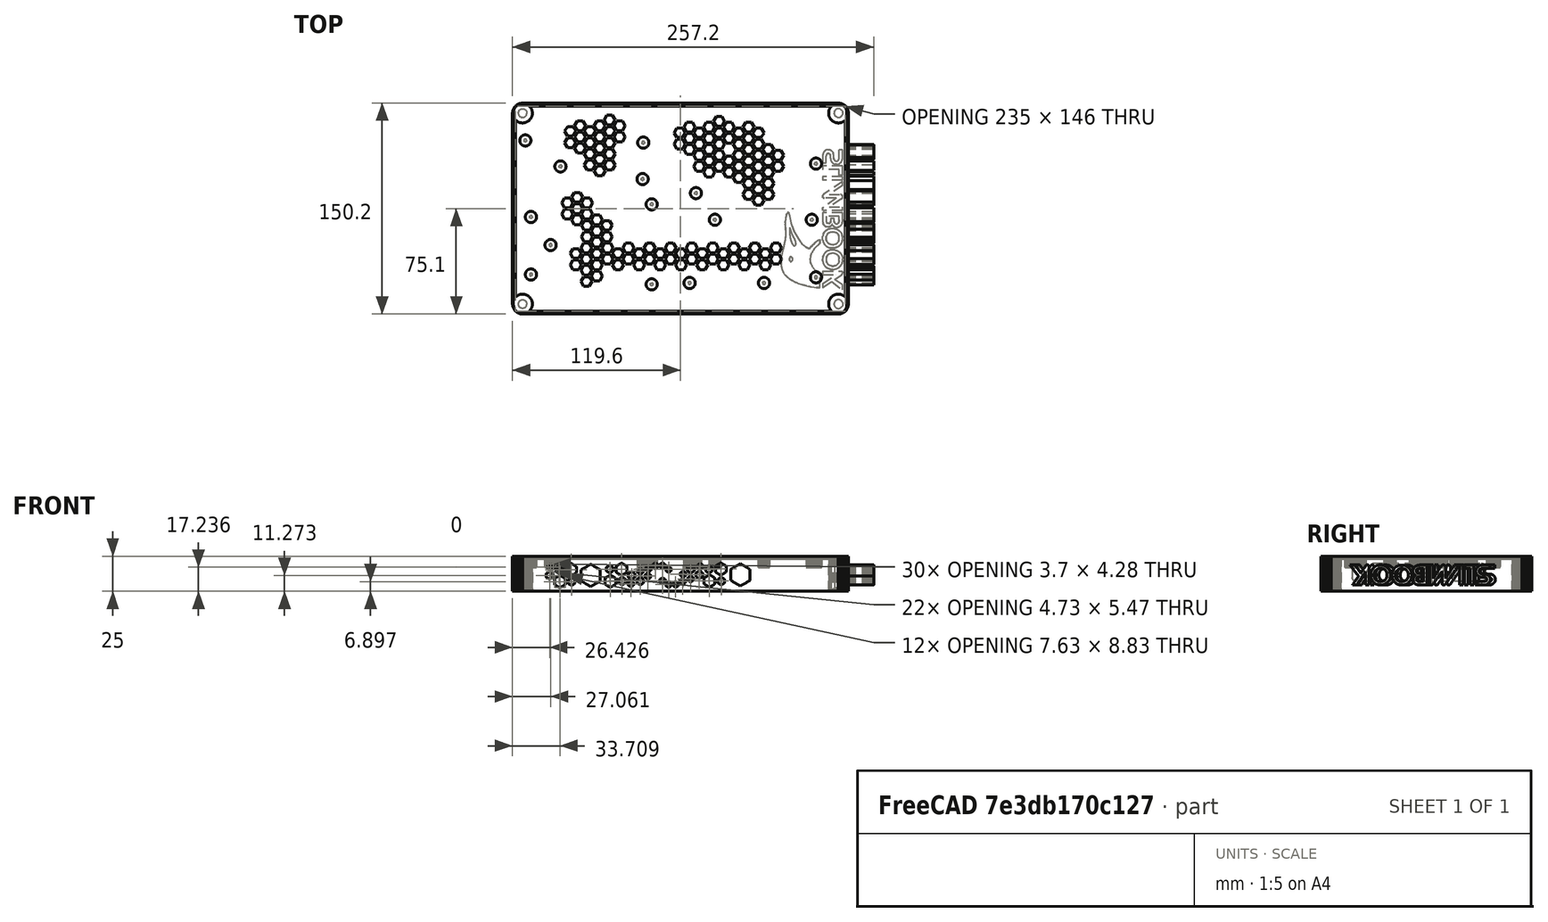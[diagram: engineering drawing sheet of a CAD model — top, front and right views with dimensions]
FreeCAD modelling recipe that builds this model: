
FCSTD DOCUMENT  (FreeCAD 0.21R33771 (Git))
Label: CAJA_slimbook
License: All rights reserved
LicenseURL: http://en.wikipedia.org/wiki/All_rights_reserved
objects: Part::Feature×108, Part::Extrusion×84, Part::Face×22, Part::Cut×8, Part::MultiFuse×5
note: 227 computed .brp shape members not serialized (recipe doc carries the construction recipe); baked Part::Feature solids carry a one-line shape summary decoded from their .brp

FEATURE [Part::Feature] path4723020
  shape: bbox 20.8 x 14.35 x 2.667e-07 mm, 0 faces, 0 solids (baked)
FEATURE [Part::Face] Face
  FaceMakerClass = Part::FaceMakerBullseye
  Sources = -> [path4723020]
FEATURE [Part::Extrusion] Extrude101
  Base = -> Face
  Dir = (0,0,1)
  DirMode = 2
  FaceMakerClass = Part::FaceMakerBullseye
  LengthFwd = 20
  LengthRev = 0
  Placement = pos=(235.5,118.54,-29.31) rot=(0.57735,-0.57735,0.57735;4.18879rad)
  Solid = false
  Symmetric = false
FEATURE [Part::Feature] path4723021
  shape: bbox 13.53 x 14.33 x 2.667e-07 mm, 0 faces, 0 solids (baked)
FEATURE [Part::Face] Face016
  FaceMakerClass = Part::FaceMakerBullseye
  Sources = -> [path4723021]
FEATURE [Part::Extrusion] Extrude102
  Base = -> Face016
  Dir = (0,0,1)
  DirMode = 2
  FaceMakerClass = Part::FaceMakerBullseye
  LengthFwd = 20
  LengthRev = 0
  Placement = pos=(235.5,118.54,-29.31) rot=(0.57735,-0.57735,0.57735;4.18879rad)
  Solid = false
  Symmetric = false
FEATURE [Part::Feature] path4723022
  shape: bbox 14.02 x 14.18 x 2.667e-07 mm, 0 faces, 0 solids (baked)
FEATURE [Part::Face] Face024
  FaceMakerClass = Part::FaceMakerBullseye
  Sources = -> [path4723022]
FEATURE [Part::Feature] path4723023
  shape: bbox 10.29 x 14.24 x 2.667e-07 mm, 0 faces, 0 solids (baked)
FEATURE [Part::Face] Face022
  FaceMakerClass = Part::FaceMakerBullseye
  Sources = -> [path4723023]
FEATURE [Part::Feature] path4723024
  shape: bbox 10.44 x 14.24 x 2.667e-07 mm, 0 faces, 0 solids (baked)
FEATURE [Part::Face] Face021
  FaceMakerClass = Part::FaceMakerBullseye
  Sources = -> [path4723024]
FEATURE [Part::Extrusion] Extrude106
  Base = -> Face021
  Dir = (0,0,1)
  DirMode = 2
  FaceMakerClass = Part::FaceMakerBullseye
  LengthFwd = 20
  LengthRev = 0
  Placement = pos=(235.5,118.54,-29.31) rot=(0.57735,-0.57735,0.57735;4.18879rad)
  Solid = false
  Symmetric = false
FEATURE [Part::Feature] path4723025
  shape: bbox 6.55 x 14.24 x 2.667e-07 mm, 0 faces, 0 solids (baked)
FEATURE [Part::Face] Face019
  FaceMakerClass = Part::FaceMakerBullseye
  Sources = -> [path4723025]
FEATURE [Part::Extrusion] Extrude104
  Base = -> Face019
  Dir = (0,0,1)
  DirMode = 2
  FaceMakerClass = Part::FaceMakerBullseye
  LengthFwd = 20
  LengthRev = 0
  Placement = pos=(235.5,118.54,-29.31) rot=(0.57735,-0.57735,0.57735;4.18879rad)
  Solid = false
  Symmetric = false
FEATURE [Part::Feature] path4723026
  shape: bbox 2.568 x 14.24 x 2.667e-07 mm, 0 faces, 0 solids (baked)
FEATURE [Part::Face] Face020
  FaceMakerClass = Part::FaceMakerBullseye
  Sources = -> [path4723026]
FEATURE [Part::Extrusion] Extrude105
  Base = -> Face020
  Dir = (0,0,1)
  DirMode = 2
  FaceMakerClass = Part::FaceMakerBullseye
  LengthFwd = 20
  LengthRev = 0
  Placement = pos=(235.5,118.54,-29.31) rot=(0.57735,-0.57735,0.57735;4.18879rad)
  Solid = false
  Symmetric = false
FEATURE [Part::Feature] path4723027  label="O"
  shape: bbox 14.02 x 14.24 x 2.667e-07 mm, 0 faces, 0 solids (baked)
FEATURE [Part::Face] Face018
  FaceMakerClass = Part::FaceMakerBullseye
  Sources = -> [path4723027]
FEATURE [Part::Feature] path4723028  label="b"
  shape: bbox 5.247 x 9.291 x 2.667e-07 mm, 0 faces, 0 solids (baked)
FEATURE [Part::Face] Face023
  FaceMakerClass = Part::FaceMakerBullseye
  Sources = -> [path4723028]
FEATURE [Part::Cut] Cut042
  Base = -> Face022
  Refine = true
  Tool = -> Face023
FEATURE [Part::Extrusion] Extrude107
  Base = -> Cut042
  Dir = (0,0,1)
  DirMode = 2
  FaceMakerClass = Part::FaceMakerBullseye
  LengthFwd = 20
  LengthRev = 0
  Placement = pos=(235.5,118.54,-29.31) rot=(0.57735,-0.57735,0.57735;4.18879rad)
  Solid = false
  Symmetric = false
FEATURE [Part::Feature] path4723029  label="oo"
  shape: bbox 9.343 x 9.236 x 2.667e-07 mm, 0 faces, 0 solids (baked)
FEATURE [Part::Face] Face025
  FaceMakerClass = Part::FaceMakerBullseye
  Sources = -> [path4723029]
FEATURE [Part::Cut] Cut043
  Base = -> Face024
  Refine = true
  Tool = -> Face025
FEATURE [Part::Extrusion] Extrude108
  Base = -> Cut043
  Dir = (0,0,1)
  DirMode = 2
  FaceMakerClass = Part::FaceMakerBullseye
  LengthFwd = 20
  LengthRev = 0
  Placement = pos=(235.5,118.54,-29.31) rot=(0.57735,-0.57735,0.57735;4.18879rad)
  Solid = false
  Symmetric = false
FEATURE [Part::Feature] path4723030
  shape: bbox 9.342 x 9.272 x 2.667e-07 mm, 0 faces, 0 solids (baked)
FEATURE [Part::Face] Face017  label="o"
  FaceMakerClass = Part::FaceMakerBullseye
  Sources = -> [path4723030]
FEATURE [Part::Cut] Cut041
  Base = -> Face018
  Refine = true
  Tool = -> Face017
FEATURE [Part::Extrusion] Extrude103
  Base = -> Cut041
  Dir = (0,0,1)
  DirMode = 2
  FaceMakerClass = Part::FaceMakerBullseye
  LengthFwd = 20
  LengthRev = 0
  Placement = pos=(235.5,118.54,-29.31) rot=(0.57735,-0.57735,0.57735;4.18879rad)
  Solid = false
  Symmetric = false
FEATURE [Part::MultiFuse] Fusion028  label="palabra"
  Placement = pos=(0.5,3.5,0) rot=(0,0,1;0rad)
  Refine = true
  Shapes = -> [Extrude101,Extrude102,Extrude103,Extrude104,Extrude105,Extrude106,Extrude107,Extrude108]
FEATURE [Part::Feature] path4723031
  shape: bbox 20.8 x 14.35 x 2.667e-07 mm, 0 faces, 0 solids (baked)
FEATURE [Part::Face] Face026
  FaceMakerClass = Part::FaceMakerBullseye
  Sources = -> [path4723031]
FEATURE [Part::Extrusion] Extrude109
  Base = -> Face026
  Dir = (0,0,1)
  DirMode = 2
  FaceMakerClass = Part::FaceMakerBullseye
  LengthFwd = 20
  LengthRev = 0
  Placement = pos=(235.5,118.54,-29.31) rot=(0.57735,-0.57735,0.57735;4.18879rad)
  Solid = false
  Symmetric = false
FEATURE [Part::Feature] path4723032
  shape: bbox 13.53 x 14.33 x 2.667e-07 mm, 0 faces, 0 solids (baked)
FEATURE [Part::Face] Face027
  FaceMakerClass = Part::FaceMakerBullseye
  Sources = -> [path4723032]
FEATURE [Part::Extrusion] Extrude110
  Base = -> Face027
  Dir = (0,0,1)
  DirMode = 2
  FaceMakerClass = Part::FaceMakerBullseye
  LengthFwd = 20
  LengthRev = 0
  Placement = pos=(235.5,118.54,-29.31) rot=(0.57735,-0.57735,0.57735;4.18879rad)
  Solid = false
  Symmetric = false
FEATURE [Part::Feature] path4723033
  shape: bbox 14.02 x 14.18 x 2.667e-07 mm, 0 faces, 0 solids (baked)
FEATURE [Part::Face] Face035
  FaceMakerClass = Part::FaceMakerBullseye
  Sources = -> [path4723033]
FEATURE [Part::Feature] path4723034
  shape: bbox 10.29 x 14.24 x 2.667e-07 mm, 0 faces, 0 solids (baked)
FEATURE [Part::Face] Face033
  FaceMakerClass = Part::FaceMakerBullseye
  Sources = -> [path4723034]
FEATURE [Part::Feature] path4723035
  shape: bbox 10.44 x 14.24 x 2.667e-07 mm, 0 faces, 0 solids (baked)
FEATURE [Part::Face] Face032
  FaceMakerClass = Part::FaceMakerBullseye
  Sources = -> [path4723035]
FEATURE [Part::Extrusion] Extrude114
  Base = -> Face032
  Dir = (0,0,1)
  DirMode = 2
  FaceMakerClass = Part::FaceMakerBullseye
  LengthFwd = 20
  LengthRev = 0
  Placement = pos=(235.5,118.54,-29.31) rot=(0.57735,-0.57735,0.57735;4.18879rad)
  Solid = false
  Symmetric = false
FEATURE [Part::Feature] path4723036
  shape: bbox 6.55 x 14.24 x 2.667e-07 mm, 0 faces, 0 solids (baked)
FEATURE [Part::Face] Face030
  FaceMakerClass = Part::FaceMakerBullseye
  Sources = -> [path4723036]
FEATURE [Part::Extrusion] Extrude112
  Base = -> Face030
  Dir = (0,0,1)
  DirMode = 2
  FaceMakerClass = Part::FaceMakerBullseye
  LengthFwd = 20
  LengthRev = 0
  Placement = pos=(235.5,118.54,-29.31) rot=(0.57735,-0.57735,0.57735;4.18879rad)
  Solid = false
  Symmetric = false
FEATURE [Part::Feature] path4723037
  shape: bbox 2.568 x 14.24 x 2.667e-07 mm, 0 faces, 0 solids (baked)
FEATURE [Part::Face] Face031
  FaceMakerClass = Part::FaceMakerBullseye
  Sources = -> [path4723037]
FEATURE [Part::Extrusion] Extrude113
  Base = -> Face031
  Dir = (0,0,1)
  DirMode = 2
  FaceMakerClass = Part::FaceMakerBullseye
  LengthFwd = 20
  LengthRev = 0
  Placement = pos=(235.5,118.54,-29.31) rot=(0.57735,-0.57735,0.57735;4.18879rad)
  Solid = false
  Symmetric = false
FEATURE [Part::Feature] path4723038  label="O001"
  shape: bbox 14.02 x 14.24 x 2.667e-07 mm, 0 faces, 0 solids (baked)
FEATURE [Part::Face] Face029
  FaceMakerClass = Part::FaceMakerBullseye
  Sources = -> [path4723038]
FEATURE [Part::Feature] path4723039  label="b001"
  shape: bbox 5.247 x 9.291 x 2.667e-07 mm, 0 faces, 0 solids (baked)
FEATURE [Part::Face] Face034
  FaceMakerClass = Part::FaceMakerBullseye
  Sources = -> [path4723039]
FEATURE [Part::Cut] Cut045
  Base = -> Face033
  Refine = true
  Tool = -> Face034
FEATURE [Part::Extrusion] Extrude115
  Base = -> Cut045
  Dir = (0,0,1)
  DirMode = 2
  FaceMakerClass = Part::FaceMakerBullseye
  LengthFwd = 20
  LengthRev = 0
  Placement = pos=(235.5,118.54,-29.31) rot=(0.57735,-0.57735,0.57735;4.18879rad)
  Solid = false
  Symmetric = false
FEATURE [Part::Feature] path4723040  label="oo001"
  shape: bbox 9.343 x 9.236 x 2.667e-07 mm, 0 faces, 0 solids (baked)
FEATURE [Part::Face] Face036
  FaceMakerClass = Part::FaceMakerBullseye
  Sources = -> [path4723040]
FEATURE [Part::Cut] Cut046
  Base = -> Face035
  Refine = true
  Tool = -> Face036
FEATURE [Part::Extrusion] Extrude116
  Base = -> Cut046
  Dir = (0,0,1)
  DirMode = 2
  FaceMakerClass = Part::FaceMakerBullseye
  LengthFwd = 20
  LengthRev = 0
  Placement = pos=(235.5,118.54,-29.31) rot=(0.57735,-0.57735,0.57735;4.18879rad)
  Solid = false
  Symmetric = false
FEATURE [Part::Feature] path4723041
  shape: bbox 9.342 x 9.272 x 2.667e-07 mm, 0 faces, 0 solids (baked)
FEATURE [Part::Face] Face028  label="o001"
  FaceMakerClass = Part::FaceMakerBullseye
  Sources = -> [path4723041]
FEATURE [Part::Cut] Cut044
  Base = -> Face029
  Refine = true
  Tool = -> Face028
FEATURE [Part::Extrusion] Extrude111
  Base = -> Cut044
  Dir = (0,0,1)
  DirMode = 2
  FaceMakerClass = Part::FaceMakerBullseye
  LengthFwd = 20
  LengthRev = 0
  Placement = pos=(235.5,118.54,-29.31) rot=(0.57735,-0.57735,0.57735;4.18879rad)
  Solid = false
  Symmetric = false
FEATURE [Part::Feature] path2951
  shape: bbox 3.697 x 4.275 x 7.858e-07 mm, 0 faces, 0 solids (baked)
FEATURE [Part::Feature] path4723042
  shape: bbox 3.697 x 4.275 x 7.858e-07 mm, 0 faces, 0 solids (baked)
FEATURE [Part::Feature] path4723043
  shape: bbox 7.634 x 8.828 x 7.858e-07 mm, 0 faces, 0 solids (baked)
FEATURE [Part::Feature] path4723044
  shape: bbox 7.634 x 8.828 x 7.858e-07 mm, 0 faces, 0 solids (baked)
FEATURE [Part::Feature] path4723045
  shape: bbox 7.635 x 8.827 x 7.858e-07 mm, 0 faces, 0 solids (baked)
FEATURE [Part::Feature] path4723046
  shape: bbox 3.697 x 4.276 x 7.858e-07 mm, 0 faces, 0 solids (baked)
FEATURE [Part::Feature] path4723047
  shape: bbox 13.76 x 15.91 x 7.858e-07 mm, 0 faces, 0 solids (baked)
FEATURE [Part::Feature] path4723048
  shape: bbox 3.697 x 4.275 x 7.858e-07 mm, 0 faces, 0 solids (baked)
FEATURE [Part::Feature] path4723049
  shape: bbox 13.76 x 15.91 x 7.858e-07 mm, 0 faces, 0 solids (baked)
FEATURE [Part::Feature] path4723050
  shape: bbox 4.734 x 5.474 x 7.858e-07 mm, 0 faces, 0 solids (baked)
FEATURE [Part::Feature] path4723051
  shape: bbox 4.734 x 5.474 x 7.858e-07 mm, 0 faces, 0 solids (baked)
FEATURE [Part::Feature] path4723052
  shape: bbox 4.734 x 5.474 x 7.858e-07 mm, 0 faces, 0 solids (baked)
FEATURE [Part::Feature] path4723053
  shape: bbox 3.697 x 4.276 x 7.858e-07 mm, 0 faces, 0 solids (baked)
FEATURE [Part::Feature] path4723054
  shape: bbox 4.734 x 5.474 x 7.858e-07 mm, 0 faces, 0 solids (baked)
FEATURE [Part::Feature] path4723055
  shape: bbox 3.697 x 4.275 x 7.858e-07 mm, 0 faces, 0 solids (baked)
FEATURE [Part::Feature] path4723056
  shape: bbox 3.697 x 4.275 x 7.858e-07 mm, 0 faces, 0 solids (baked)
FEATURE [Part::Feature] path4723057
  shape: bbox 4.734 x 5.474 x 7.858e-07 mm, 0 faces, 0 solids (baked)
FEATURE [Part::Feature] path4723058
  shape: bbox 3.697 x 4.276 x 7.858e-07 mm, 0 faces, 0 solids (baked)
FEATURE [Part::Feature] path4723059
  shape: bbox 4.734 x 5.474 x 7.858e-07 mm, 0 faces, 0 solids (baked)
FEATURE [Part::Feature] path4723060
  shape: bbox 4.734 x 5.474 x 7.858e-07 mm, 0 faces, 0 solids (baked)
FEATURE [Part::Feature] path4723061
  shape: bbox 3.697 x 4.275 x 7.858e-07 mm, 0 faces, 0 solids (baked)
FEATURE [Part::Feature] path4723062
  shape: bbox 7.634 x 8.828 x 7.858e-07 mm, 0 faces, 0 solids (baked)
FEATURE [Part::Feature] path4723063
  shape: bbox 7.634 x 8.827 x 7.858e-07 mm, 0 faces, 0 solids (baked)
FEATURE [Part::Feature] path4723064
  shape: bbox 7.634 x 8.828 x 7.858e-07 mm, 0 faces, 0 solids (baked)
FEATURE [Part::Feature] path4723065
  shape: bbox 3.697 x 4.276 x 7.858e-07 mm, 0 faces, 0 solids (baked)
FEATURE [Part::Feature] path4723066
  shape: bbox 4.734 x 5.474 x 7.858e-07 mm, 0 faces, 0 solids (baked)
FEATURE [Part::Feature] path4723067
  shape: bbox 4.734 x 5.474 x 7.858e-07 mm, 0 faces, 0 solids (baked)
FEATURE [Part::Feature] path4723068
  shape: bbox 4.734 x 5.474 x 7.858e-07 mm, 0 faces, 0 solids (baked)
FEATURE [Part::Feature] path4723069
  shape: bbox 3.697 x 4.275 x 7.858e-07 mm, 0 faces, 0 solids (baked)
FEATURE [Part::Feature] path4723070
  shape: bbox 4.734 x 5.474 x 7.858e-07 mm, 0 faces, 0 solids (baked)
FEATURE [Part::Feature] path4723071
  shape: bbox 3.697 x 4.275 x 7.858e-07 mm, 0 faces, 0 solids (baked)
FEATURE [Part::Feature] path4723072
  shape: bbox 3.697 x 4.275 x 7.858e-07 mm, 0 faces, 0 solids (baked)
FEATURE [Part::Feature] path4723073
  shape: bbox 3.697 x 4.275 x 7.858e-07 mm, 0 faces, 0 solids (baked)
FEATURE [Part::Feature] path4723074
  shape: bbox 3.697 x 4.276 x 7.858e-07 mm, 0 faces, 0 solids (baked)
FEATURE [Part::Extrusion] Extrude
  Base = -> path4723042
  Dir = (0,0,1)
  DirMode = 2
  FaceMakerClass = Part::FaceMakerBullseye
  LengthFwd = 20
  LengthRev = 0
  Solid = true
  Symmetric = false
FEATURE [Part::Extrusion] Extrude117
  Base = -> path4723043
  Dir = (0,0,1)
  DirMode = 2
  FaceMakerClass = Part::FaceMakerBullseye
  LengthFwd = 20
  LengthRev = 0
  Solid = true
  Symmetric = false
FEATURE [Part::Extrusion] Extrude118
  Base = -> path4723044
  Dir = (0,0,1)
  DirMode = 2
  FaceMakerClass = Part::FaceMakerBullseye
  LengthFwd = 20
  LengthRev = 0
  Solid = true
  Symmetric = false
FEATURE [Part::Extrusion] Extrude119
  Base = -> path4723045
  Dir = (0,0,1)
  DirMode = 2
  FaceMakerClass = Part::FaceMakerBullseye
  LengthFwd = 20
  LengthRev = 0
  Solid = true
  Symmetric = false
FEATURE [Part::Extrusion] Extrude120
  Base = -> path4723046
  Dir = (0,0,1)
  DirMode = 2
  FaceMakerClass = Part::FaceMakerBullseye
  LengthFwd = 20
  LengthRev = 0
  Solid = true
  Symmetric = false
FEATURE [Part::Extrusion] Extrude121
  Base = -> path4723047
  Dir = (0,0,1)
  DirMode = 2
  FaceMakerClass = Part::FaceMakerBullseye
  LengthFwd = 20
  LengthRev = 0
  Solid = true
  Symmetric = false
FEATURE [Part::Extrusion] Extrude122
  Base = -> path4723048
  Dir = (0,0,1)
  DirMode = 2
  FaceMakerClass = Part::FaceMakerBullseye
  LengthFwd = 20
  LengthRev = 0
  Solid = true
  Symmetric = false
FEATURE [Part::Extrusion] Extrude123
  Base = -> path4723049
  Dir = (0,0,1)
  DirMode = 2
  FaceMakerClass = Part::FaceMakerBullseye
  LengthFwd = 20
  LengthRev = 0
  Solid = true
  Symmetric = false
FEATURE [Part::Extrusion] Extrude124
  Base = -> path4723050
  Dir = (0,0,1)
  DirMode = 2
  FaceMakerClass = Part::FaceMakerBullseye
  LengthFwd = 20
  LengthRev = 0
  Solid = true
  Symmetric = false
FEATURE [Part::Extrusion] Extrude125
  Base = -> path4723051
  Dir = (0,0,1)
  DirMode = 2
  FaceMakerClass = Part::FaceMakerBullseye
  LengthFwd = 20
  LengthRev = 0
  Solid = true
  Symmetric = false
FEATURE [Part::Extrusion] Extrude126
  Base = -> path4723052
  Dir = (0,0,1)
  DirMode = 2
  FaceMakerClass = Part::FaceMakerBullseye
  LengthFwd = 20
  LengthRev = 0
  Solid = true
  Symmetric = false
FEATURE [Part::Extrusion] Extrude127
  Base = -> path4723053
  Dir = (0,0,1)
  DirMode = 2
  FaceMakerClass = Part::FaceMakerBullseye
  LengthFwd = 20
  LengthRev = 0
  Solid = true
  Symmetric = false
FEATURE [Part::Extrusion] Extrude128
  Base = -> path4723054
  Dir = (0,0,1)
  DirMode = 2
  FaceMakerClass = Part::FaceMakerBullseye
  LengthFwd = 20
  LengthRev = 0
  Solid = true
  Symmetric = false
FEATURE [Part::Extrusion] Extrude129
  Base = -> path4723055
  Dir = (0,0,1)
  DirMode = 2
  FaceMakerClass = Part::FaceMakerBullseye
  LengthFwd = 20
  LengthRev = 0
  Solid = true
  Symmetric = false
FEATURE [Part::Extrusion] Extrude130
  Base = -> path4723056
  Dir = (0,0,1)
  DirMode = 2
  FaceMakerClass = Part::FaceMakerBullseye
  LengthFwd = 20
  LengthRev = 0
  Solid = true
  Symmetric = false
FEATURE [Part::Extrusion] Extrude131
  Base = -> path4723057
  Dir = (0,0,1)
  DirMode = 2
  FaceMakerClass = Part::FaceMakerBullseye
  LengthFwd = 20
  LengthRev = 0
  Solid = true
  Symmetric = false
FEATURE [Part::Extrusion] Extrude132
  Base = -> path4723058
  Dir = (0,0,1)
  DirMode = 2
  FaceMakerClass = Part::FaceMakerBullseye
  LengthFwd = 20
  LengthRev = 0
  Solid = true
  Symmetric = false
FEATURE [Part::Extrusion] Extrude133
  Base = -> path4723059
  Dir = (0,0,1)
  DirMode = 2
  FaceMakerClass = Part::FaceMakerBullseye
  LengthFwd = 20
  LengthRev = 0
  Solid = true
  Symmetric = false
FEATURE [Part::Extrusion] Extrude134
  Base = -> path4723060
  Dir = (0,0,1)
  DirMode = 2
  FaceMakerClass = Part::FaceMakerBullseye
  LengthFwd = 20
  LengthRev = 0
  Solid = true
  Symmetric = false
FEATURE [Part::Extrusion] Extrude135
  Base = -> path4723061
  Dir = (0,0,1)
  DirMode = 2
  FaceMakerClass = Part::FaceMakerBullseye
  LengthFwd = 20
  LengthRev = 0
  Solid = true
  Symmetric = false
FEATURE [Part::Extrusion] Extrude136
  Base = -> path4723062
  Dir = (0,0,1)
  DirMode = 2
  FaceMakerClass = Part::FaceMakerBullseye
  LengthFwd = 20
  LengthRev = 0
  Solid = true
  Symmetric = false
FEATURE [Part::Extrusion] Extrude137
  Base = -> path4723063
  Dir = (0,0,1)
  DirMode = 2
  FaceMakerClass = Part::FaceMakerBullseye
  LengthFwd = 20
  LengthRev = 0
  Solid = true
  Symmetric = false
FEATURE [Part::Extrusion] Extrude138
  Base = -> path4723064
  Dir = (0,0,1)
  DirMode = 2
  FaceMakerClass = Part::FaceMakerBullseye
  LengthFwd = 20
  LengthRev = 0
  Solid = true
  Symmetric = false
FEATURE [Part::Extrusion] Extrude139
  Base = -> path4723065
  Dir = (0,0,1)
  DirMode = 2
  FaceMakerClass = Part::FaceMakerBullseye
  LengthFwd = 20
  LengthRev = 0
  Solid = true
  Symmetric = false
FEATURE [Part::Extrusion] Extrude140
  Base = -> path4723066
  Dir = (0,0,1)
  DirMode = 2
  FaceMakerClass = Part::FaceMakerBullseye
  LengthFwd = 20
  LengthRev = 0
  Solid = true
  Symmetric = false
FEATURE [Part::Extrusion] Extrude141
  Base = -> path4723067
  Dir = (0,0,1)
  DirMode = 2
  FaceMakerClass = Part::FaceMakerBullseye
  LengthFwd = 20
  LengthRev = 0
  Solid = true
  Symmetric = false
FEATURE [Part::Extrusion] Extrude142
  Base = -> path4723068
  Dir = (0,0,1)
  DirMode = 2
  FaceMakerClass = Part::FaceMakerBullseye
  LengthFwd = 20
  LengthRev = 0
  Solid = true
  Symmetric = false
FEATURE [Part::Extrusion] Extrude143
  Base = -> path4723069
  Dir = (0,0,1)
  DirMode = 2
  FaceMakerClass = Part::FaceMakerBullseye
  LengthFwd = 20
  LengthRev = 0
  Solid = true
  Symmetric = false
FEATURE [Part::Extrusion] Extrude144
  Base = -> path4723070
  Dir = (0,0,1)
  DirMode = 2
  FaceMakerClass = Part::FaceMakerBullseye
  LengthFwd = 20
  LengthRev = 0
  Solid = true
  Symmetric = false
FEATURE [Part::Extrusion] Extrude145
  Base = -> path4723071
  Dir = (0,0,1)
  DirMode = 2
  FaceMakerClass = Part::FaceMakerBullseye
  LengthFwd = 20
  LengthRev = 0
  Solid = true
  Symmetric = false
FEATURE [Part::Extrusion] Extrude146
  Base = -> path4723072
  Dir = (0,0,1)
  DirMode = 2
  FaceMakerClass = Part::FaceMakerBullseye
  LengthFwd = 20
  LengthRev = 0
  Solid = true
  Symmetric = false
FEATURE [Part::Extrusion] Extrude147
  Base = -> path4723073
  Dir = (0,0,1)
  DirMode = 2
  FaceMakerClass = Part::FaceMakerBullseye
  LengthFwd = 20
  LengthRev = 0
  Solid = true
  Symmetric = false
FEATURE [Part::Extrusion] Extrude148
  Base = -> path4723074
  Dir = (0,0,1)
  DirMode = 2
  FaceMakerClass = Part::FaceMakerBullseye
  LengthFwd = 20
  LengthRev = 0
  Solid = true
  Symmetric = false
FEATURE [Part::Extrusion] Extrude149
  Base = -> path2951
  Dir = (0,0,1)
  DirMode = 2
  FaceMakerClass = Part::FaceMakerBullseye
  LengthFwd = 20
  LengthRev = 0
  Solid = true
  Symmetric = false
FEATURE [Part::MultiFuse] Fusion  label="palitos_cortos"
  Placement = pos=(105,160,17) rot=(1,0,0;1.5708rad)
  Refine = true
  Shapes = -> [Extrude,Extrude117,Extrude118,Extrude119,Extrude120,Extrude121,Extrude122,Extrude123,Extrude124,Extrude125,Extrude126,Extrude127,Extrude128,Extrude129,Extrude130,Extrude131,Extrude132,Extrude133,Extrude134,Extrude135,Extrude136,Extrude137,Extrude138,Extrude139,Extrude140,Extrude141,Extrude142,Extrude143,Extrude144,Extrude145,Extrude146,Extrude147,Extrude148,Extrude149]
  expr: .Placement.Rotation.Angle = 90
FEATURE [Part::Feature] path4723109
  shape: bbox 3.697 x 4.275 x 7.858e-07 mm, 0 faces, 0 solids (baked)
FEATURE [Part::Extrusion] Extrude217
  Base = -> path4723109
  Dir = (0,0,1)
  DirMode = 2
  FaceMakerClass = Part::FaceMakerBullseye
  LengthFwd = 20
  LengthRev = 0
  Solid = true
  Symmetric = false
FEATURE [Part::Feature] path4723110
  shape: bbox 3.697 x 4.275 x 7.858e-07 mm, 0 faces, 0 solids (baked)
FEATURE [Part::Extrusion] Extrude184
  Base = -> path4723110
  Dir = (0,0,1)
  DirMode = 2
  FaceMakerClass = Part::FaceMakerBullseye
  LengthFwd = 20
  LengthRev = 0
  Solid = true
  Symmetric = false
FEATURE [Part::Feature] path4723111
  shape: bbox 7.634 x 8.828 x 7.858e-07 mm, 0 faces, 0 solids (baked)
FEATURE [Part::Extrusion] Extrude185
  Base = -> path4723111
  Dir = (0,0,1)
  DirMode = 2
  FaceMakerClass = Part::FaceMakerBullseye
  LengthFwd = 20
  LengthRev = 0
  Solid = true
  Symmetric = false
FEATURE [Part::Feature] path4723112
  shape: bbox 7.634 x 8.828 x 7.858e-07 mm, 0 faces, 0 solids (baked)
FEATURE [Part::Extrusion] Extrude186
  Base = -> path4723112
  Dir = (0,0,1)
  DirMode = 2
  FaceMakerClass = Part::FaceMakerBullseye
  LengthFwd = 20
  LengthRev = 0
  Solid = true
  Symmetric = false
FEATURE [Part::Feature] path4723113
  shape: bbox 7.635 x 8.827 x 7.858e-07 mm, 0 faces, 0 solids (baked)
FEATURE [Part::Extrusion] Extrude187
  Base = -> path4723113
  Dir = (0,0,1)
  DirMode = 2
  FaceMakerClass = Part::FaceMakerBullseye
  LengthFwd = 20
  LengthRev = 0
  Solid = true
  Symmetric = false
FEATURE [Part::Feature] path4723114
  shape: bbox 3.697 x 4.276 x 7.858e-07 mm, 0 faces, 0 solids (baked)
FEATURE [Part::Extrusion] Extrude188
  Base = -> path4723114
  Dir = (0,0,1)
  DirMode = 2
  FaceMakerClass = Part::FaceMakerBullseye
  LengthFwd = 20
  LengthRev = 0
  Solid = true
  Symmetric = false
FEATURE [Part::Feature] path4723115
  shape: bbox 13.76 x 15.91 x 7.858e-07 mm, 0 faces, 0 solids (baked)
FEATURE [Part::Extrusion] Extrude189
  Base = -> path4723115
  Dir = (0,0,1)
  DirMode = 2
  FaceMakerClass = Part::FaceMakerBullseye
  LengthFwd = 20
  LengthRev = 0
  Solid = true
  Symmetric = false
FEATURE [Part::Feature] path4723116
  shape: bbox 3.697 x 4.275 x 7.858e-07 mm, 0 faces, 0 solids (baked)
FEATURE [Part::Extrusion] Extrude190
  Base = -> path4723116
  Dir = (0,0,1)
  DirMode = 2
  FaceMakerClass = Part::FaceMakerBullseye
  LengthFwd = 20
  LengthRev = 0
  Solid = true
  Symmetric = false
FEATURE [Part::Feature] path4723117
  shape: bbox 13.76 x 15.91 x 7.858e-07 mm, 0 faces, 0 solids (baked)
FEATURE [Part::Extrusion] Extrude191
  Base = -> path4723117
  Dir = (0,0,1)
  DirMode = 2
  FaceMakerClass = Part::FaceMakerBullseye
  LengthFwd = 20
  LengthRev = 0
  Solid = true
  Symmetric = false
FEATURE [Part::Feature] path4723118
  shape: bbox 4.734 x 5.474 x 7.858e-07 mm, 0 faces, 0 solids (baked)
FEATURE [Part::Extrusion] Extrude192
  Base = -> path4723118
  Dir = (0,0,1)
  DirMode = 2
  FaceMakerClass = Part::FaceMakerBullseye
  LengthFwd = 20
  LengthRev = 0
  Solid = true
  Symmetric = false
FEATURE [Part::Feature] path4723119
  shape: bbox 4.734 x 5.474 x 7.858e-07 mm, 0 faces, 0 solids (baked)
FEATURE [Part::Extrusion] Extrude193
  Base = -> path4723119
  Dir = (0,0,1)
  DirMode = 2
  FaceMakerClass = Part::FaceMakerBullseye
  LengthFwd = 20
  LengthRev = 0
  Solid = true
  Symmetric = false
FEATURE [Part::Feature] path4723120
  shape: bbox 4.734 x 5.474 x 7.858e-07 mm, 0 faces, 0 solids (baked)
FEATURE [Part::Extrusion] Extrude194
  Base = -> path4723120
  Dir = (0,0,1)
  DirMode = 2
  FaceMakerClass = Part::FaceMakerBullseye
  LengthFwd = 20
  LengthRev = 0
  Solid = true
  Symmetric = false
FEATURE [Part::Feature] path4723121
  shape: bbox 3.697 x 4.276 x 7.858e-07 mm, 0 faces, 0 solids (baked)
FEATURE [Part::Extrusion] Extrude195
  Base = -> path4723121
  Dir = (0,0,1)
  DirMode = 2
  FaceMakerClass = Part::FaceMakerBullseye
  LengthFwd = 20
  LengthRev = 0
  Solid = true
  Symmetric = false
FEATURE [Part::Feature] path4723122
  shape: bbox 4.734 x 5.474 x 7.858e-07 mm, 0 faces, 0 solids (baked)
FEATURE [Part::Extrusion] Extrude196
  Base = -> path4723122
  Dir = (0,0,1)
  DirMode = 2
  FaceMakerClass = Part::FaceMakerBullseye
  LengthFwd = 20
  LengthRev = 0
  Solid = true
  Symmetric = false
FEATURE [Part::Feature] path4723123
  shape: bbox 3.697 x 4.275 x 7.858e-07 mm, 0 faces, 0 solids (baked)
FEATURE [Part::Extrusion] Extrude197
  Base = -> path4723123
  Dir = (0,0,1)
  DirMode = 2
  FaceMakerClass = Part::FaceMakerBullseye
  LengthFwd = 20
  LengthRev = 0
  Solid = true
  Symmetric = false
FEATURE [Part::Feature] path4723124
  shape: bbox 3.697 x 4.275 x 7.858e-07 mm, 0 faces, 0 solids (baked)
FEATURE [Part::Extrusion] Extrude198
  Base = -> path4723124
  Dir = (0,0,1)
  DirMode = 2
  FaceMakerClass = Part::FaceMakerBullseye
  LengthFwd = 20
  LengthRev = 0
  Solid = true
  Symmetric = false
FEATURE [Part::Feature] path4723125
  shape: bbox 4.734 x 5.474 x 7.858e-07 mm, 0 faces, 0 solids (baked)
FEATURE [Part::Extrusion] Extrude199
  Base = -> path4723125
  Dir = (0,0,1)
  DirMode = 2
  FaceMakerClass = Part::FaceMakerBullseye
  LengthFwd = 20
  LengthRev = 0
  Solid = true
  Symmetric = false
FEATURE [Part::Feature] path4723126
  shape: bbox 3.697 x 4.276 x 7.858e-07 mm, 0 faces, 0 solids (baked)
FEATURE [Part::Extrusion] Extrude200
  Base = -> path4723126
  Dir = (0,0,1)
  DirMode = 2
  FaceMakerClass = Part::FaceMakerBullseye
  LengthFwd = 20
  LengthRev = 0
  Solid = true
  Symmetric = false
FEATURE [Part::Feature] path4723127
  shape: bbox 4.734 x 5.474 x 7.858e-07 mm, 0 faces, 0 solids (baked)
FEATURE [Part::Extrusion] Extrude201
  Base = -> path4723127
  Dir = (0,0,1)
  DirMode = 2
  FaceMakerClass = Part::FaceMakerBullseye
  LengthFwd = 20
  LengthRev = 0
  Solid = true
  Symmetric = false
FEATURE [Part::Feature] path4723128
  shape: bbox 4.734 x 5.474 x 7.858e-07 mm, 0 faces, 0 solids (baked)
FEATURE [Part::Extrusion] Extrude202
  Base = -> path4723128
  Dir = (0,0,1)
  DirMode = 2
  FaceMakerClass = Part::FaceMakerBullseye
  LengthFwd = 20
  LengthRev = 0
  Solid = true
  Symmetric = false
FEATURE [Part::Feature] path4723129
  shape: bbox 3.697 x 4.275 x 7.858e-07 mm, 0 faces, 0 solids (baked)
FEATURE [Part::Extrusion] Extrude203
  Base = -> path4723129
  Dir = (0,0,1)
  DirMode = 2
  FaceMakerClass = Part::FaceMakerBullseye
  LengthFwd = 20
  LengthRev = 0
  Solid = true
  Symmetric = false
FEATURE [Part::Feature] path4723130
  shape: bbox 7.634 x 8.828 x 7.858e-07 mm, 0 faces, 0 solids (baked)
FEATURE [Part::Extrusion] Extrude204
  Base = -> path4723130
  Dir = (0,0,1)
  DirMode = 2
  FaceMakerClass = Part::FaceMakerBullseye
  LengthFwd = 20
  LengthRev = 0
  Solid = true
  Symmetric = false
FEATURE [Part::Feature] path4723131
  shape: bbox 7.634 x 8.827 x 7.858e-07 mm, 0 faces, 0 solids (baked)
FEATURE [Part::Extrusion] Extrude205
  Base = -> path4723131
  Dir = (0,0,1)
  DirMode = 2
  FaceMakerClass = Part::FaceMakerBullseye
  LengthFwd = 20
  LengthRev = 0
  Solid = true
  Symmetric = false
FEATURE [Part::Feature] path4723132
  shape: bbox 7.634 x 8.828 x 7.858e-07 mm, 0 faces, 0 solids (baked)
FEATURE [Part::Extrusion] Extrude206
  Base = -> path4723132
  Dir = (0,0,1)
  DirMode = 2
  FaceMakerClass = Part::FaceMakerBullseye
  LengthFwd = 20
  LengthRev = 0
  Solid = true
  Symmetric = false
FEATURE [Part::Feature] path4723133
  shape: bbox 3.697 x 4.276 x 7.858e-07 mm, 0 faces, 0 solids (baked)
FEATURE [Part::Extrusion] Extrude207
  Base = -> path4723133
  Dir = (0,0,1)
  DirMode = 2
  FaceMakerClass = Part::FaceMakerBullseye
  LengthFwd = 20
  LengthRev = 0
  Solid = true
  Symmetric = false
FEATURE [Part::Feature] path4723134
  shape: bbox 4.734 x 5.474 x 7.858e-07 mm, 0 faces, 0 solids (baked)
FEATURE [Part::Extrusion] Extrude208
  Base = -> path4723134
  Dir = (0,0,1)
  DirMode = 2
  FaceMakerClass = Part::FaceMakerBullseye
  LengthFwd = 20
  LengthRev = 0
  Solid = true
  Symmetric = false
FEATURE [Part::Feature] path4723135
  shape: bbox 4.734 x 5.474 x 7.858e-07 mm, 0 faces, 0 solids (baked)
FEATURE [Part::Extrusion] Extrude209
  Base = -> path4723135
  Dir = (0,0,1)
  DirMode = 2
  FaceMakerClass = Part::FaceMakerBullseye
  LengthFwd = 20
  LengthRev = 0
  Solid = true
  Symmetric = false
FEATURE [Part::Feature] path4723136
  shape: bbox 4.734 x 5.474 x 7.858e-07 mm, 0 faces, 0 solids (baked)
FEATURE [Part::Extrusion] Extrude210
  Base = -> path4723136
  Dir = (0,0,1)
  DirMode = 2
  FaceMakerClass = Part::FaceMakerBullseye
  LengthFwd = 20
  LengthRev = 0
  Solid = true
  Symmetric = false
FEATURE [Part::Feature] path4723137
  shape: bbox 3.697 x 4.275 x 7.858e-07 mm, 0 faces, 0 solids (baked)
FEATURE [Part::Extrusion] Extrude211
  Base = -> path4723137
  Dir = (0,0,1)
  DirMode = 2
  FaceMakerClass = Part::FaceMakerBullseye
  LengthFwd = 20
  LengthRev = 0
  Solid = true
  Symmetric = false
FEATURE [Part::Feature] path4723138
  shape: bbox 4.734 x 5.474 x 7.858e-07 mm, 0 faces, 0 solids (baked)
FEATURE [Part::Extrusion] Extrude212
  Base = -> path4723138
  Dir = (0,0,1)
  DirMode = 2
  FaceMakerClass = Part::FaceMakerBullseye
  LengthFwd = 20
  LengthRev = 0
  Solid = true
  Symmetric = false
FEATURE [Part::Feature] path4723139
  shape: bbox 3.697 x 4.275 x 7.858e-07 mm, 0 faces, 0 solids (baked)
FEATURE [Part::Extrusion] Extrude213
  Base = -> path4723139
  Dir = (0,0,1)
  DirMode = 2
  FaceMakerClass = Part::FaceMakerBullseye
  LengthFwd = 20
  LengthRev = 0
  Solid = true
  Symmetric = false
FEATURE [Part::Feature] path4723140
  shape: bbox 3.697 x 4.275 x 7.858e-07 mm, 0 faces, 0 solids (baked)
FEATURE [Part::Extrusion] Extrude214
  Base = -> path4723140
  Dir = (0,0,1)
  DirMode = 2
  FaceMakerClass = Part::FaceMakerBullseye
  LengthFwd = 20
  LengthRev = 0
  Solid = true
  Symmetric = false
FEATURE [Part::Feature] path4723141
  shape: bbox 3.697 x 4.275 x 7.858e-07 mm, 0 faces, 0 solids (baked)
FEATURE [Part::Extrusion] Extrude215
  Base = -> path4723141
  Dir = (0,0,1)
  DirMode = 2
  FaceMakerClass = Part::FaceMakerBullseye
  LengthFwd = 20
  LengthRev = 0
  Solid = true
  Symmetric = false
FEATURE [Part::Feature] path4723142
  shape: bbox 3.697 x 4.276 x 7.858e-07 mm, 0 faces, 0 solids (baked)
FEATURE [Part::Extrusion] Extrude216
  Base = -> path4723142
  Dir = (0,0,1)
  DirMode = 2
  FaceMakerClass = Part::FaceMakerBullseye
  LengthFwd = 20
  LengthRev = 0
  Solid = true
  Symmetric = false
FEATURE [Part::MultiFuse] Fusion032  label="palitos_cortos001"
  Placement = pos=(105,8,17) rot=(1,0,0;1.5708rad)
  Refine = true
  Shapes = -> [Extrude184,Extrude185,Extrude186,Extrude187,Extrude188,Extrude189,Extrude190,Extrude191,Extrude192,Extrude193,Extrude194,Extrude195,Extrude196,Extrude197,Extrude198,Extrude199,Extrude200,Extrude201,Extrude202,Extrude203,Extrude204,Extrude205,Extrude206,Extrude207,Extrude208,Extrude209,Extrude210,Extrude211,Extrude212,Extrude213,Extrude214,Extrude215,Extrude216,Extrude217]
  expr: .Placement.Rotation.Angle = 90
FEATURE [Part::MultiFuse] Fusion033  label="palitos_cortos_laterales"
  Refine = true
  Shapes = -> [Fusion032,Fusion]
FEATURE [Part::Feature] Component018_solid  label="Component018 (Solid)"
  shape: bbox 239.2 x 150.2 x 25 mm, 4116 faces (baked)
FEATURE [Part::Cut] Cut  label="lado-palabra"
  Base = -> Component018_solid
  Refine = true
  Tool = -> Fusion028
FEATURE [Part::Cut] Cut050  label="lados-cortados"
  Base = -> Cut
  Refine = true
  Tool = -> Fusion033
FEATURE [Part::Feature] Component020_solid  label="Component020 (Solid)"
  shape: bbox 8 x 7.998 x 8 mm, 1004 faces (baked)
FEATURE [Part::Feature] Component019_solid001  label="base (Solid)"
  shape: bbox 237.5 x 149 x 2 mm, 12018 faces (baked)
FEATURE [Part::Feature] Component021_solid  label="Component021 (Solid)"
  shape: bbox 8 x 7.998 x 8 mm, 1004 faces (baked)
FEATURE [Part::Feature] Component022_solid  label="Component022 (Solid)"
  shape: bbox 8 x 7.998 x 8 mm, 1004 faces (baked)
FEATURE [Part::Feature] Component023_solid  label="Component023 (Solid)"
  shape: bbox 8 x 7.998 x 8 mm, 1004 faces (baked)
FEATURE [Part::Feature] Component024_solid  label="Component024 (Solid)"
  shape: bbox 8 x 7.998 x 8 mm, 1004 faces (baked)
FEATURE [Part::Feature] Component025_solid  label="Component025 (Solid)"
  shape: bbox 8 x 7.998 x 8 mm, 1004 faces (baked)
FEATURE [Part::Feature] Component026_solid  label="Component026 (Solid)"
  shape: bbox 8 x 7.998 x 8 mm, 1004 faces (baked)
FEATURE [Part::Feature] Component027_solid  label="Component027 (Solid)"
  shape: bbox 8 x 7.998 x 8 mm, 1004 faces (baked)
FEATURE [Part::Feature] Component028_solid  label="Component028 (Solid)"
  shape: bbox 8 x 7.998 x 8 mm, 1004 faces (baked)
FEATURE [Part::Feature] Component029_solid  label="Component029 (Solid)"
  shape: bbox 8 x 7.998 x 8 mm, 1004 faces (baked)
FEATURE [Part::Feature] Component030_solid  label="Component030 (Solid)"
  shape: bbox 8 x 7.998 x 8 mm, 1004 faces (baked)
FEATURE [Part::Feature] Component031_solid  label="Component031 (Solid)"
  shape: bbox 8 x 7.998 x 8 mm, 1004 faces (baked)
FEATURE [Part::Feature] Component032_solid  label="Component032 (Solid)"
  shape: bbox 8 x 7.998 x 8 mm, 1004 faces (baked)
FEATURE [Part::Feature] Component033_solid  label="Component033 (Solid)"
  shape: bbox 8 x 7.998 x 8 mm, 1004 faces (baked)
FEATURE [Part::Feature] Component034_solid  label="Component034 (Solid)"
  shape: bbox 8 x 7.998 x 8 mm, 1004 faces (baked)
FEATURE [Part::Feature] Component035_solid  label="Component035 (Solid)"
  shape: bbox 8 x 7.998 x 8 mm, 1004 faces (baked)
FEATURE [Part::MultiFuse] Fusion029  label="palabra001"
  Placement = pos=(-0.4,0,0) rot=(0,0,1;0rad)
  Refine = true
  Shapes = -> [Extrude109,Extrude110,Extrude111,Extrude112,Extrude113,Extrude114,Extrude115,Extrude116]
